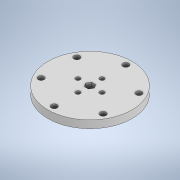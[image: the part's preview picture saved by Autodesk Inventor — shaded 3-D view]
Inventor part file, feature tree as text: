
AUTODESK INVENTOR PART (.ipt)
format: ipt  version: 2020.2 (Build 242310000, 310)  size: 151,040 bytes
history: native  units: in
note: dims shown in document units (in); Inventor stores cm internally (conversion verified against a paired STEP export)
features: extrude x4, sketch x3, pattern_circular x1
ambient origin geometry x8: Origin, YZ Plane, XZ Plane, XY Plane, X Axis, Y Axis, Z Axis, Center Point
bodies: Solid1 (feature_tree)
feature tree (8):
  extrude  "Extrusion1"  Depth=0.2in TaperAngle=0.0deg
  extrude  "Extrusion9"  Depth=0.2in
  extrude  "Extrusion5"  TaperAngle=0.0deg  [1 undecoded]
  extrude  "Extrusion10"  Depth=0.315in
  pattern_circular  "Circular Pattern4"  [2 undecoded]
  sketch  "Sketch1"  dims[d0=2.2in d1=0.2in d2=0.0in]
  sketch  "Sketch12"  dims[d15=1.0in d16=0.0in d33=0.2in]
  sketch  "Sketch13"  dims[d34=1.0in d35=0.0in d42=0.0in d43=0.315in d44=0.12in d45=1.0in d46=0.0in d47=1.5748in d48=360.0deg d10=0.5in d11=0.0344in d12=0.5in d13=0.0344in d27=0.5in d28=0.0344in d29=0.5in d30=0.0344in]
note: 3 required parameter values undecoded (feature->parameter linkage not recoverable at this tier; creation-order binding heuristic only, values carry confidence <= 0.55)
